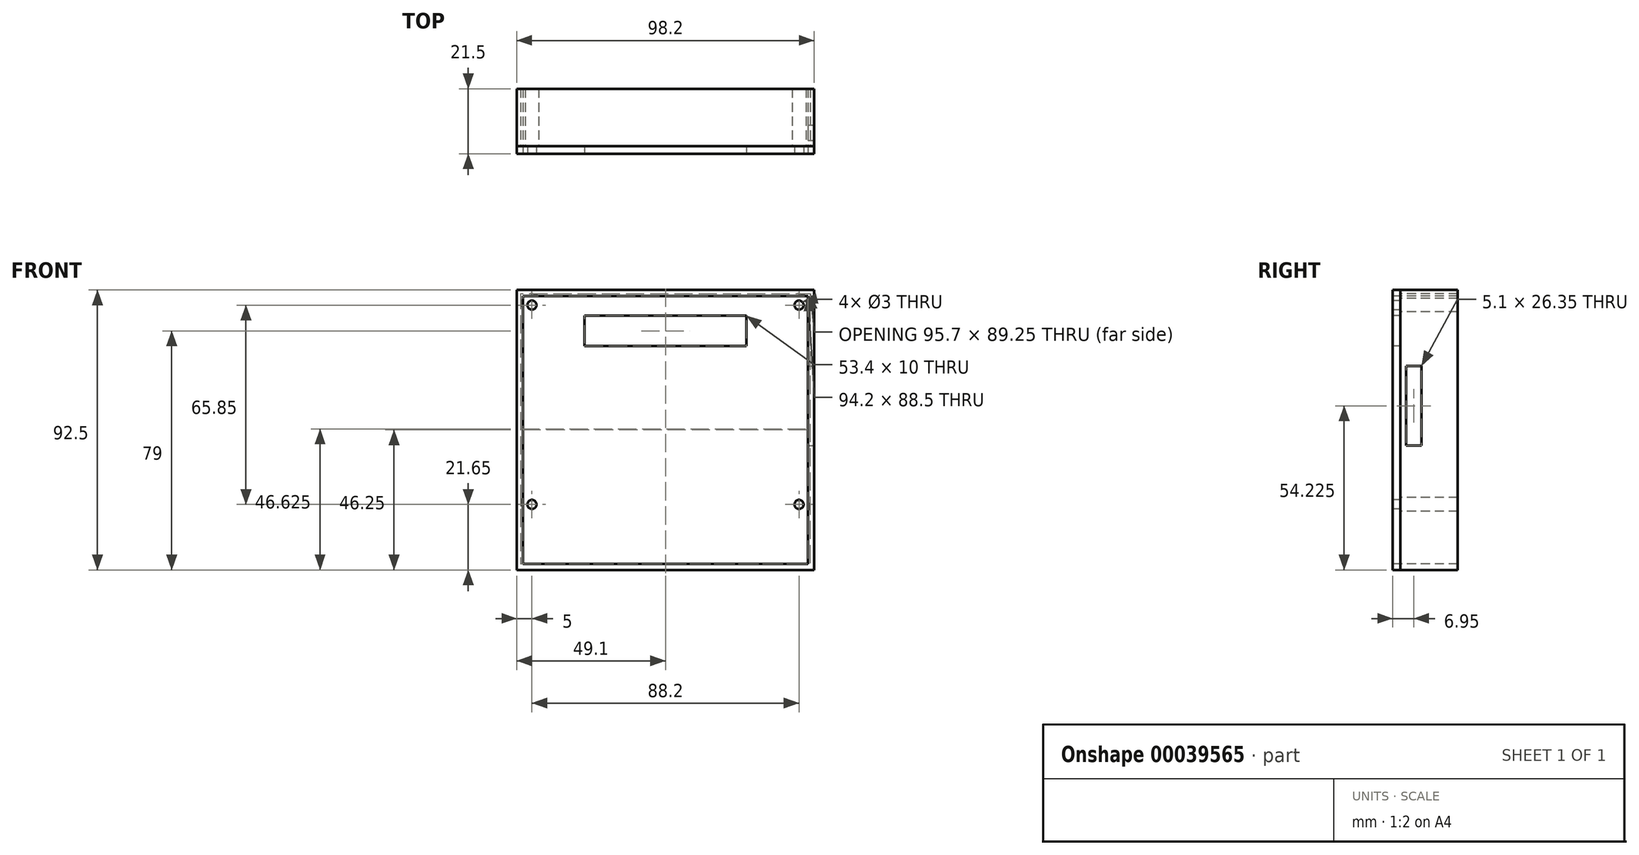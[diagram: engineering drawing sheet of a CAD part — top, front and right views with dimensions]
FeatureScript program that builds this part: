
annotation { "Feature Type Name" : "Feature", "Feature Type Description" : "" }
export const myFeature = defineFeature(function(context is Context, id is Id, definition is map)
    precondition{}
    {
        {
            var Q0;
            Q0=qCreatedBy(makeId("Front.planeOp"),FACE);
            var sketch = newSketch(context, id + "F0", { "sketchPlane" : qUnion([Q0])});
            skLineSegment(sketch, "E0.bottom", {"start": v(0, 0) * mm, "end": v(94.2, 0) * mm});
            skLineSegment(sketch, "E0.top", {"start": v(0, 88.5) * mm, "end": v(94.2, 88.5) * mm});
            skLineSegment(sketch, "E0.left", {"start": v(0, 0) * mm, "end": v(0, 88.5) * mm});
            skLineSegment(sketch, "E0.right", {"start": v(94.2, 0) * mm, "end": v(94.2, 88.5) * mm});
            skLineSegment(sketch, "E1", {"start": v(94.2, 85.5) * mm, "end": v(91.2, 85.5) * mm, "construction": true});
            skLineSegment(sketch, "E2", {"start": v(91.2, 85.5) * mm, "end": v(91.2, 88.5) * mm, "construction": true});
            skLineSegment(sketch, "E3", {"start": v(0, 3) * mm, "end": v(3, 3) * mm, "construction": true});
            skLineSegment(sketch, "E4", {"start": v(3, 3) * mm, "end": v(3, 0) * mm, "construction": true});
            skLineSegment(sketch, "E5.bottom", {"start": v(91.2, 85.5) * mm, "end": v(3, 85.5) * mm, "construction": true});
            skLineSegment(sketch, "E5.top", {"start": v(91.2, 3) * mm, "end": v(3, 3) * mm, "construction": true});
            skLineSegment(sketch, "E5.left", {"start": v(91.2, 85.5) * mm, "end": v(91.2, 3) * mm, "construction": true});
            skLineSegment(sketch, "E5.right", {"start": v(3, 85.5) * mm, "end": v(3, 3) * mm, "construction": true});
            skCircle(sketch, "E6", {"center": v(3, 85.5) * mm, "radius": 1.5 * mm});
            skCircle(sketch, "E7", {"center": v(91.2, 85.5) * mm, "radius": 1.5 * mm});
            skLineSegment(sketch, "E8", {"start": v(97.23, 0) * mm, "end": v(97.23, 19.65) * mm, "construction": true});
            skLineSegment(sketch, "E9", {"start": v(97.23, 19.65) * mm, "end": v(-23.24, 19.65) * mm, "construction": true});
            skCircle(sketch, "E10", {"center": v(91.2, 19.65) * mm, "radius": 1.5 * mm});
            skCircle(sketch, "E11", {"center": v(3, 19.65) * mm, "radius": 1.5 * mm});
            skLineSegment(sketch, "E12", {"start": v(99.42, 88.5) * mm, "end": v(99.42, 72) * mm, "construction": true});
            skLineSegment(sketch, "E13", {"start": v(99.42, 72) * mm, "end": v(94.2, 72) * mm, "construction": true});
            skLineSegment(sketch, "E14", {"start": v(94.2, 72) * mm, "end": v(73.8, 72) * mm, "construction": true});
            skLineSegment(sketch, "E15", {"start": v(0, 72) * mm, "end": v(20.4, 72) * mm, "construction": true});
            skLineSegment(sketch, "E16", {"start": v(20.4, 72) * mm, "end": v(73.8, 72) * mm});
            skLineSegment(sketch, "E17", {"start": v(73.8, 82) * mm, "end": v(20.4, 82) * mm});
            skLineSegment(sketch, "E18", {"start": v(20.4, 82) * mm, "end": v(20.4, 72) * mm});
            skLineSegment(sketch, "E19", {"start": v(73.8, 82) * mm, "end": v(73.8, 72) * mm});
            skSolve(sketch);
        }
        {
            var Q0;
            Q0=qSketchRegion(id+"F0",true);
            extrude(context, id + "F1", {"entities" : qUnion([Q0]), "oppositeDirection" : true, "depth" : 2.5 * mm});
        }
        {
            var Q0;
            Q0=makeQuery(id+"F1.opExtrude","CAP_FACE",FACE,{"disambiguationData":[OSD([sQuery(id+"F0.wireOp",EDGE,"E0.bottom"),sQuery(id+"F0.wireOp",EDGE,"E0.top"),sQuery(id+"F0.wireOp",EDGE,"E0.left"),sQuery(id+"F0.wireOp",EDGE,"E0.right"),sQuery(id+"F0.wireOp",EDGE,"E6"),sQuery(id+"F0.wireOp",EDGE,"E7"),sQuery(id+"F0.wireOp",EDGE,"E10"),sQuery(id+"F0.wireOp",EDGE,"E11"),sQuery(id+"F0.wireOp",EDGE,"E16"),sQuery(id+"F0.wireOp",EDGE,"E17"),sQuery(id+"F0.wireOp",EDGE,"E18"),sQuery(id+"F0.wireOp",EDGE,"E19")])],"isStart":false});
            var sketch = newSketch(context, id + "F2", { "sketchPlane" : qUnion([Q0])});
            skLineSegment(sketch, "E20", {"start": v(-94.2, 88.5) * mm, "end": v(-96.2, 88.5) * mm, "construction": true});
            skLineSegment(sketch, "E21", {"start": v(-96.2, 88.5) * mm, "end": v(-96.2, 90.5) * mm, "construction": true});
            skLineSegment(sketch, "E22", {"start": v(0, 0) * mm, "end": v(2, 0) * mm, "construction": true});
            skLineSegment(sketch, "E23", {"start": v(2, 0) * mm, "end": v(2, -2) * mm, "construction": true});
            skLineSegment(sketch, "E24.bottom", {"start": v(-96.2, 90.5) * mm, "end": v(2, 90.5) * mm});
            skLineSegment(sketch, "E24.top", {"start": v(-96.2, -2) * mm, "end": v(2, -2) * mm});
            skLineSegment(sketch, "E24.left", {"start": v(-96.2, 90.5) * mm, "end": v(-96.2, -2) * mm});
            skLineSegment(sketch, "E24.right", {"start": v(2, 90.5) * mm, "end": v(2, -2) * mm});
            skLineSegment(sketch, "E25.bottom", {"start": v(-94.2, 88.5) * mm, "end": v(-5.25, 88.5) * mm});
            skLineSegment(sketch, "E25.top", {"start": v(-94.2, 0) * mm, "end": v(0, 0) * mm});
            skLineSegment(sketch, "E25.left", {"start": v(-94.2, 88.5) * mm, "end": v(-94.2, 0) * mm});
            skLineSegment(sketch, "E25.right", {"start": v(0, 88.5) * mm, "end": v(0, 0) * mm});
            skArc(sketch, "E26", {"start": v(0, 17.4) * mm, "mid": v(0.75, 19.65) * mm, "end": v(0, 21.9) * mm});
            skArc(sketch, "E27", {"start": v(0, 21.9) * mm, "mid": v(-6.75, 19.65) * mm, "end": v(0, 17.4) * mm, "construction": true});
            skArc(sketch, "E28", {"start": v(0, 83.25) * mm, "mid": v(0.75, 85.5) * mm, "end": v(0, 87.75) * mm});
            skArc(sketch, "E29", {"start": v(0, 87.75) * mm, "mid": v(-0.35, 88.15) * mm, "end": v(-0.75, 88.5) * mm, "construction": true});
            skArc(sketch, "E30", {"start": v(-0.75, 88.5) * mm, "mid": v(-3, 89.25) * mm, "end": v(-5.25, 88.5) * mm});
            skLineSegment(sketch, "E31", {"start": v(-5.25, 88.5) * mm, "end": v(0, 88.5) * mm});
            skArc(sketch, "E32", {"start": v(-88.95, 88.5) * mm, "mid": v(-91.2, 89.25) * mm, "end": v(-93.45, 88.5) * mm});
            skArc(sketch, "E33", {"start": v(-93.45, 88.5) * mm, "mid": v(-93.83, 88.17) * mm, "end": v(-94.17, 87.8) * mm, "construction": true});
            skArc(sketch, "E34", {"start": v(-94.17, 87.8) * mm, "mid": v(-94.95, 85.53) * mm, "end": v(-94.2, 83.25) * mm});
            skArc(sketch, "E35", {"start": v(-94.2, 83.25) * mm, "mid": v(-88.55, 82.85) * mm, "end": v(-88.95, 88.5) * mm, "construction": true});
            skArc(sketch, "E36", {"start": v(-94.2, 17.4) * mm, "mid": v(-87.45, 19.65) * mm, "end": v(-94.2, 21.9) * mm, "construction": true});
            skArc(sketch, "E37", {"start": v(-94.2, 21.9) * mm, "mid": v(-94.95, 19.65) * mm, "end": v(-94.2, 17.4) * mm});
            skLineSegment(sketch, "E38", {"start": v(-94.2, 17.4) * mm, "end": v(-94.2, 21.9) * mm});
            skLineSegment(sketch, "E39", {"start": v(0, 17.4) * mm, "end": v(0, 21.9) * mm});
            skArc(sketch, "E40", {"start": v(-5.25, 88.5) * mm, "mid": v(-5.65, 82.85) * mm, "end": v(0, 83.25) * mm, "construction": true});
            skLineSegment(sketch, "E41", {"start": v(0, 83.25) * mm, "end": v(0, 87.75) * mm});
            skLineSegment(sketch, "E42", {"start": v(-5.25, 88.5) * mm, "end": v(-0.75, 88.5) * mm});
            skLineSegment(sketch, "E43", {"start": v(-88.95, 88.5) * mm, "end": v(-93.45, 88.5) * mm});
            skLineSegment(sketch, "E44", {"start": v(-94.2, 83.25) * mm, "end": v(-94.17, 87.8) * mm});
            skSolve(sketch);
        }
        {
            var Q0;
            Q0=qSketchRegion(id+"F2",true);
            extrude(context, id + "F3", {"entities" : qUnion([Q0]), "operationType" : NewBodyOperationType.ADD, "depth" : 19 * mm});
        }
        {
            var Q0;
            Q0=makeQuery(id+"F3.opExtrude","CAP_FACE",FACE,{"disambiguationData":[OSD([sQuery(id+"F2.wireOp",EDGE,"E24.bottom"),sQuery(id+"F2.wireOp",EDGE,"E24.top"),sQuery(id+"F2.wireOp",EDGE,"E24.left"),sQuery(id+"F2.wireOp",EDGE,"E24.right"),sQuery(id+"F2.wireOp",EDGE,"E25.bottom"),sQuery(id+"F2.wireOp",EDGE,"E25.top"),sQuery(id+"F2.wireOp",EDGE,"E25.left"),sQuery(id+"F2.wireOp",EDGE,"E25.right"),sQuery(id+"F2.wireOp",EDGE,"E26"),sQuery(id+"F2.wireOp",EDGE,"E28"),sQuery(id+"F2.wireOp",EDGE,"E30"),sQuery(id+"F2.wireOp",EDGE,"E31"),sQuery(id+"F2.wireOp",EDGE,"E32"),sQuery(id+"F2.wireOp",EDGE,"E34"),sQuery(id+"F2.wireOp",EDGE,"E37")])],"isStart":true});
            var sketch = newSketch(context, id + "F4", { "sketchPlane" : qUnion([Q0])});
            skLineSegment(sketch, "E45.bottom", {"start": v(96.2, 90.5) * mm, "end": v(-2, 90.5) * mm});
            skLineSegment(sketch, "E45.top", {"start": v(96.2, -2) * mm, "end": v(-2, -2) * mm});
            skLineSegment(sketch, "E45.left", {"start": v(96.2, 90.5) * mm, "end": v(96.2, -2) * mm});
            skLineSegment(sketch, "E45.right", {"start": v(-2, 90.5) * mm, "end": v(-2, -2) * mm});
            skLineSegment(sketch, "E46.bottom", {"start": v(0, 0) * mm, "end": v(94.2, 0) * mm});
            skLineSegment(sketch, "E46.top", {"start": v(0, 88.5) * mm, "end": v(94.2, 88.5) * mm});
            skLineSegment(sketch, "E46.left", {"start": v(0, 0) * mm, "end": v(0, 88.5) * mm});
            skLineSegment(sketch, "E46.right", {"start": v(94.2, 0) * mm, "end": v(94.2, 88.5) * mm});
            skSolve(sketch);
        }
        {
            var Q0;
            Q0=qSketchRegion(id+"F4",true);
            extrude(context, id + "F5", {"entities" : qUnion([Q0]), "depth" : 2.5 * mm});
        }
        {
            var Q0;
            Q0=makeQuery(id+"F3.opExtrude","SWEPT_FACE",FACE,{"disambiguationData":[OSD([sQuery(id+"F2.wireOp",EDGE,"E24.left")])]});
            var sketch = newSketch(context, id + "F6", { "sketchPlane" : qUnion([Q0])});
            skLineSegment(sketch, "E47", {"start": v(24.54, 90.5) * mm, "end": v(24.54, 88.5) * mm, "construction": true});
            skLineSegment(sketch, "E48", {"start": v(24.54, 88.5) * mm, "end": v(21.5, 88.5) * mm, "construction": true});
            skLineSegment(sketch, "E49", {"start": v(21.5, 88.5) * mm, "end": v(4.4, 88.5) * mm, "construction": true});
            skLineSegment(sketch, "E50", {"start": v(4.4, 88.5) * mm, "end": v(4.4, 65.4) * mm, "construction": true});
            skLineSegment(sketch, "E51", {"start": v(4.4, 65.4) * mm, "end": v(4.4, 39.05) * mm});
            skLineSegment(sketch, "E52", {"start": v(4.4, 39.05) * mm, "end": v(9.5, 39.05) * mm});
            skLineSegment(sketch, "E53", {"start": v(9.5, 39.05) * mm, "end": v(9.5, 65.4) * mm});
            skLineSegment(sketch, "E54", {"start": v(9.5, 65.4) * mm, "end": v(4.4, 65.4) * mm});
            skSolve(sketch);
        }
        {
            var Q0;
            Q0=qSketchRegion(id+"F6",true);
            extrude(context, id + "F7", {"entities" : qUnion([Q0]), "operationType" : NewBodyOperationType.REMOVE, "oppositeDirection" : true, "depth" : 2.1 * mm});
        }
    });
